# Revit family: LZPT22
name_source: partatom
category: Lighting Fixtures
units: mm (PartAtom-declared; Revit-internal decimal feet)

## family parameters
Cut with Voids When Loaded = No
Host = Face
Light Source = Yes
OmniClass Number = 23.80.70.11
OmniClass Title = Luminaries for Internal Lighting
Part Type = Normal
Room Calculation Point = No
Round Connector Dimension = Use Diameter
Shared = No

## types (3) — shared parameters
Color Filter = 16777215
Default Elevation = 48 "
Description = LED Zero Plenum® Troffer
Dimming Lamp Color Temperature Shift = <None>
Emit Shape Visible in Rendering = No
Emit from Rectangle Length = 22 "
Emit from Rectangle Width = 22 "
Lamp = LED Lamp
Load Classification = Lighting
Manufacturer = Columbia Lighting
Material Finish = Paint - White
Model = LZPT 22
Opal lens = Glass
Tilt Angle = -90.00°
URL = https://www.currentlighting.com
Wattage Comments = 18W-43W
zzLength1 = 5.625 "

## per-type parameters (varying)
| type | Apparent Load | Is 120V | Is 277V | Photometric Web File | Voltage | Watts |
| LZPT22-35HLG-LSRS-EU | 35 VA | No | Yes | LZPT22-35HLG-LSRS-EU.ies | 277 V | 35 W |
| LZPT22-35LWG-LSRS-EU | 26 VA | No | Yes | LZPT22-35LWG-LSRS-EU.ies | 277 V | 26 W |
| LZPT22-35MLG-LSRS-EU | 31 VA | Yes | No | LZPT22-35MLG-LSRS-EU.ies | 120 V | 31 W |

## geometry (parser evidence)
native form markers: Sweep x4
no freeform markers — native parametric forms only
